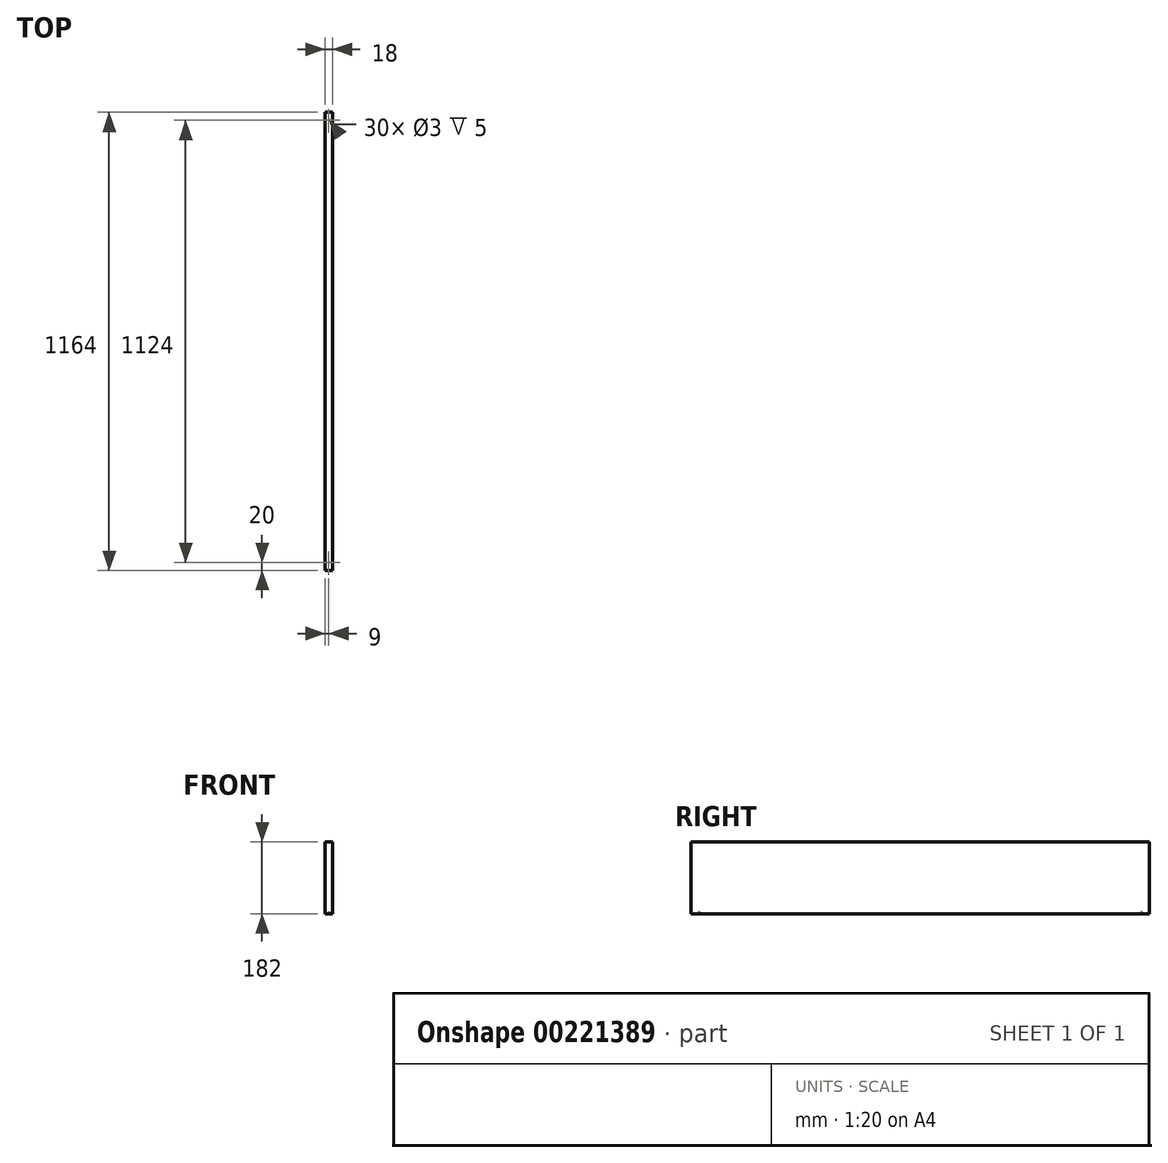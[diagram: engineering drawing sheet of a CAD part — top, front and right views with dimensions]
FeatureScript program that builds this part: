
annotation { "Feature Type Name" : "Feature", "Feature Type Description" : "" }
export const myFeature = defineFeature(function(context is Context, id is Id, definition is map)
    precondition{}
    {
        {
            var Q0;
            Q0=qCreatedBy(makeId("Right.planeOp"),FACE);
            var sketch = newSketch(context, id + "F0", { "sketchPlane" : qUnion([Q0])});
            skLineSegment(sketch, "E0.bottom", {"start": v(582, -91) * mm, "end": v(-582, -91) * mm});
            skLineSegment(sketch, "E0.top", {"start": v(582, 91) * mm, "end": v(-582, 91) * mm});
            skLineSegment(sketch, "E0.left", {"start": v(582, -91) * mm, "end": v(582, 91) * mm});
            skLineSegment(sketch, "E0.right", {"start": v(-582, -91) * mm, "end": v(-582, 91) * mm});
            skPoint(sketch, "E0.middle", {"position": v(0, 0) * mm});
            skSolve(sketch);
        }
        {
            var Q0;
            Q0 = qSketchRegion(id + "F0", true);
            extrude(context, id + "F1", {"entities" : qUnion([Q0]), "depth" : 18 * mm});
        }
        {
            var Q0;
            Q0=makeQuery(id+"F1.opExtrude","SWEPT_FACE",FACE,{"disambiguationData":[OSD([sQuery(id+"F0.wireOp",EDGE,"E0.bottom")])]});
            var sketch = newSketch(context, id + "F2", { "sketchPlane" : qUnion([Q0])});
            skCircle(sketch, "E1", {"center": v(9, 562) * mm, "radius": 1.5 * mm});
            skPoint(sketch, "E1.centerSnap0", {"position": v(9, 582) * mm});
            skCircle(sketch, "E2", {"center": v(9, -562) * mm, "radius": 1.5 * mm});
            skPoint(sketch, "E2.centerSnap0", {"position": v(9, -582) * mm});
            skSolve(sketch);
        }
        {
            var Q0;
            Q0 = qSketchRegion(id + "F2", true);
            extrude(context, id + "F3", {"entities" : qUnion([Q0]), "operationType" : NewBodyOperationType.REMOVE, "oppositeDirection" : true, "depth" : 5 * mm});
        }
    });
